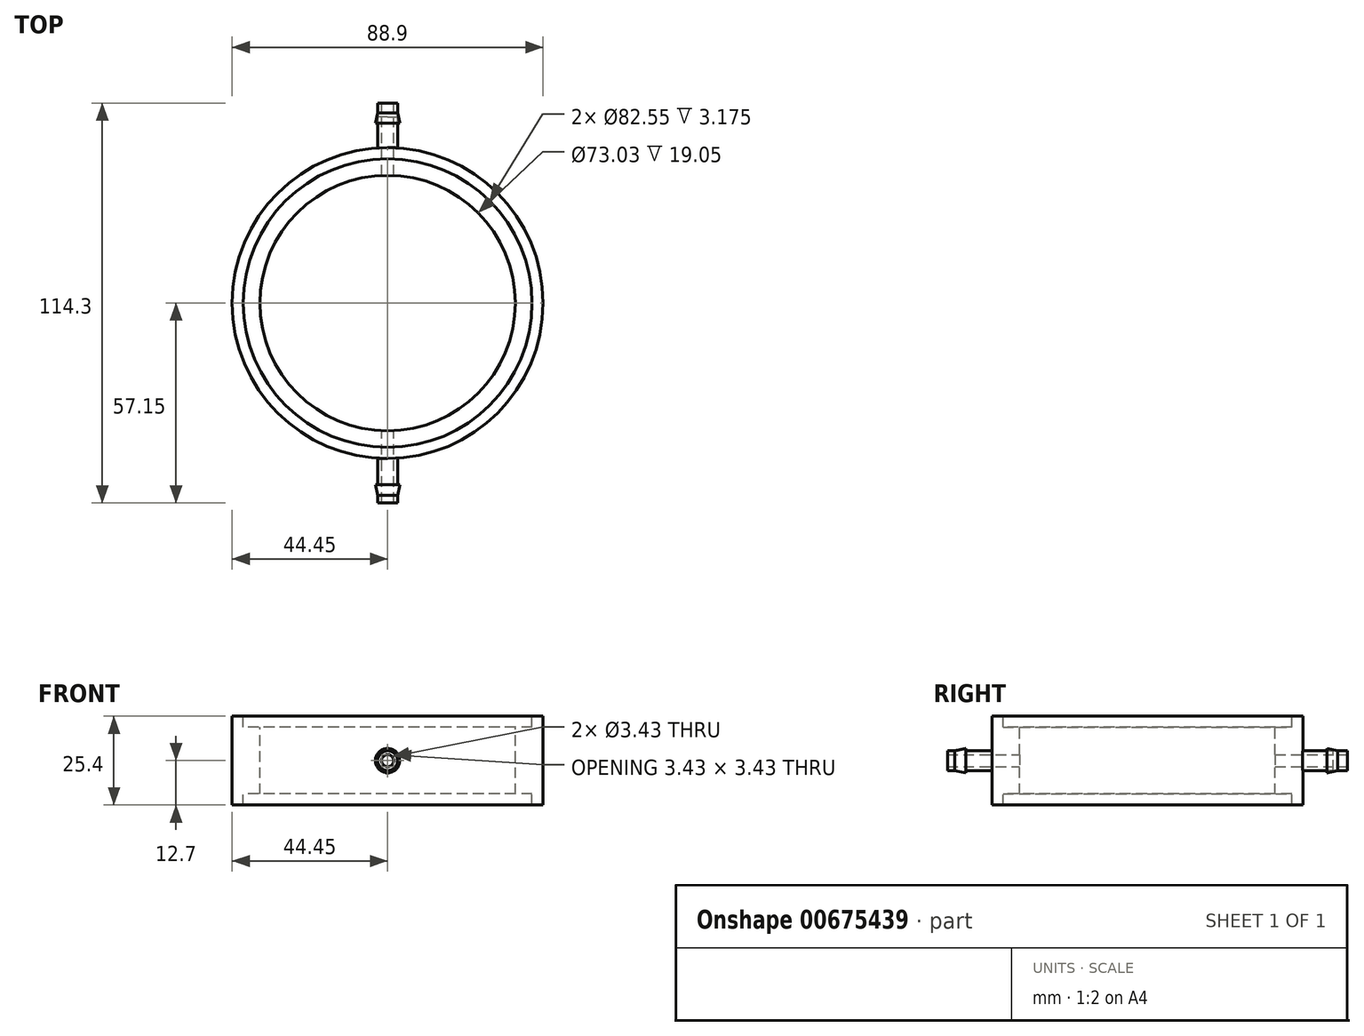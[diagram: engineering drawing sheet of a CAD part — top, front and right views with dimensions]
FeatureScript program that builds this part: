
annotation { "Feature Type Name" : "Feature", "Feature Type Description" : "" }
export const myFeature = defineFeature(function(context is Context, id is Id, definition is map)
    precondition{}
    {
        {
            var Q0;
            Q0=qCreatedBy(makeId("Top.planeOp"),FACE);
            var sketch = newSketch(context, id + "F0", { "sketchPlane" : qUnion([Q0])});
            skCircle(sketch, "E0", {"center": v(0, 0) * mm, "radius": 44.45 * mm});
            skSolve(sketch);
        }
        {
            var Q0;
            Q0=makeQuery(id+"F0.imprint","IMPRINT",FACE,{"disambiguationData":[TD([[makeQuery(id+"F0.imprint","IMPRINT",EDGE,{"derivedFrom":sQuery(id+"F0.wireOp",EDGE,"E0")}),1.0]])]});
            extrude(context, id + "F1", {"entities" : qUnion([Q0]), "endBound" : BoundingType.SYMMETRIC, "depth" : 25.4 * mm, "offsetDistance" : 25.4 * mm});
        }
        {
            var Q0;
            Q0=qCreatedBy(makeId("Top.planeOp"),FACE);
            var sketch = newSketch(context, id + "F2", { "sketchPlane" : qUnion([Q0])});
            skCircle(sketch, "E1", {"center": v(0, 0) * mm, "radius": 41.27 * mm});
            skSolve(sketch);
        }
        {
            var Q0;
            Q0 = qSketchRegion(id + "F2", true);
            extrude(context, id + "F3", {"entities" : qUnion([Q0]), "operationType" : NewBodyOperationType.REMOVE, "endBound" : BoundingType.SYMMETRIC, "oppositeDirection" : true, "depth" : 25.4 * mm, "offsetDistance" : 25.4 * mm});
        }
        {
            var Q0;
            Q0=qCreatedBy(makeId("Top.planeOp"),FACE);
            var sketch = newSketch(context, id + "F4", { "sketchPlane" : qUnion([Q0])});
            skCircle(sketch, "E2", {"center": v(0, 0) * mm, "radius": 41.28 * mm});
            skSolve(sketch);
        }
        {
            var Q0;
            Q0 = qSketchRegion(id + "F4", true);
            extrude(context, id + "F5", {"entities" : qUnion([Q0]), "operationType" : NewBodyOperationType.ADD, "endBound" : BoundingType.SYMMETRIC, "depth" : 19.05 * mm, "offsetDistance" : 25.4 * mm});
        }
        {
            var Q0;
            Q0=qCreatedBy(makeId("Top.planeOp"),FACE);
            var sketch = newSketch(context, id + "F6", { "sketchPlane" : qUnion([Q0])});
            skCircle(sketch, "E3", {"center": v(0, 0) * mm, "radius": 36.51 * mm});
            skSolve(sketch);
        }
        {
            var Q0;
            Q0=qCreatedBy(makeId("Front.planeOp"),FACE);
            var sketch = newSketch(context, id + "F7", { "sketchPlane" : qUnion([Q0])});
            skCircle(sketch, "E4", {"center": v(0, 0) * mm, "radius": 2.83 * mm});
            skSolve(sketch);
        }
        {
            var Q0;
            Q0 = qSketchRegion(id + "F7", true);
            extrude(context, id + "F8", {"entities" : qUnion([Q0]), "operationType" : NewBodyOperationType.ADD, "endBound" : BoundingType.SYMMETRIC, "depth" : 114.3 * mm, "offsetDistance" : 25.4 * mm});
        }
        {
            var Q0;
            Q0=qCreatedBy(makeId("Right.planeOp"),FACE);
            var sketch = newSketch(context, id + "F9", { "sketchPlane" : qUnion([Q0])});
            skLineSegment(sketch, "E5", {"start": v(-55.04, -2.83) * mm, "end": v(-51.93, -3.47) * mm});
            skLineSegment(sketch, "E6", {"start": v(-51.93, -3.47) * mm, "end": v(-51.93, -2.83) * mm});
            skLineSegment(sketch, "E7", {"start": v(-51.93, -2.83) * mm, "end": v(-55.04, -2.83) * mm});
            skSolve(sketch);
        }
        {
            var Q0;
            Q0=makeQuery(id+"F9.imprint","IMPRINT",FACE,{"disambiguationData":[TD([[makeQuery(id+"F9.imprint","IMPRINT",EDGE,{"derivedFrom":sQuery(id+"F9.wireOp",EDGE,"E5")}),1.0]])]});
            var Q1;
            Q1=makeQuery(id+"F8.opExtrude","CAP_EDGE",EDGE,{"disambiguationData":[OSD([sQuery(id+"F7.wireOp",EDGE,"E4")])],"isStart":false});
            revolve(context, id + "F10", {"operationType" : NewBodyOperationType.ADD, "entities" : qUnion([Q0]), "axis" : qUnion([Q1]), "revolveType" : RevolveType.FULL});
        }
        {
            var Q0;
            Q0=qCreatedBy(makeId("Front.planeOp"),FACE);
            var sketch = newSketch(context, id + "F11", { "sketchPlane" : qUnion([Q0])});
            skCircle(sketch, "E8", {"center": v(0, 0) * mm, "radius": 1.71 * mm});
            skSolve(sketch);
        }
        {
            var Q0;
            Q0 = qSketchRegion(id + "F11", true);
            extrude(context, id + "F12", {"entities" : qUnion([Q0]), "operationType" : NewBodyOperationType.REMOVE, "endBound" : BoundingType.SYMMETRIC, "depth" : 114.3 * mm, "offsetDistance" : 25.4 * mm});
        }
        {
            var Q0;
            Q0=qCreatedBy(makeId("Right.planeOp"),FACE);
            var sketch = newSketch(context, id + "F13", { "sketchPlane" : qUnion([Q0])});
            skLineSegment(sketch, "E9", {"start": v(54.52, -2.8) * mm, "end": v(51.42, -3.51) * mm});
            skLineSegment(sketch, "E10", {"start": v(51.42, -3.51) * mm, "end": v(51.42, -2.87) * mm});
            skLineSegment(sketch, "E11", {"start": v(51.42, -2.87) * mm, "end": v(54.52, -2.8) * mm});
            skSolve(sketch);
        }
        {
            var Q0;
            Q0=makeQuery(id+"F13.imprint","IMPRINT",FACE,{"disambiguationData":[TD([[makeQuery(id+"F13.imprint","IMPRINT",EDGE,{"derivedFrom":sQuery(id+"F13.wireOp",EDGE,"E9")}),-1.0]])]});
            var Q1;
            Q1=makeQuery(id+"F8.opExtrude","CAP_EDGE",EDGE,{"disambiguationData":[OSD([sQuery(id+"F7.wireOp",EDGE,"E4")])],"isStart":true});
            revolve(context, id + "F14", {"operationType" : NewBodyOperationType.ADD, "entities" : qUnion([Q0]), "axis" : qUnion([Q1]), "revolveType" : RevolveType.FULL});
        }
        {
            var Q0;
            Q0 = qSketchRegion(id + "F6", true);
            extrude(context, id + "F15", {"entities" : qUnion([Q0]), "operationType" : NewBodyOperationType.REMOVE, "endBound" : BoundingType.SYMMETRIC, "oppositeDirection" : true, "depth" : 25.4 * mm, "offsetDistance" : 25.4 * mm});
        }
    });
